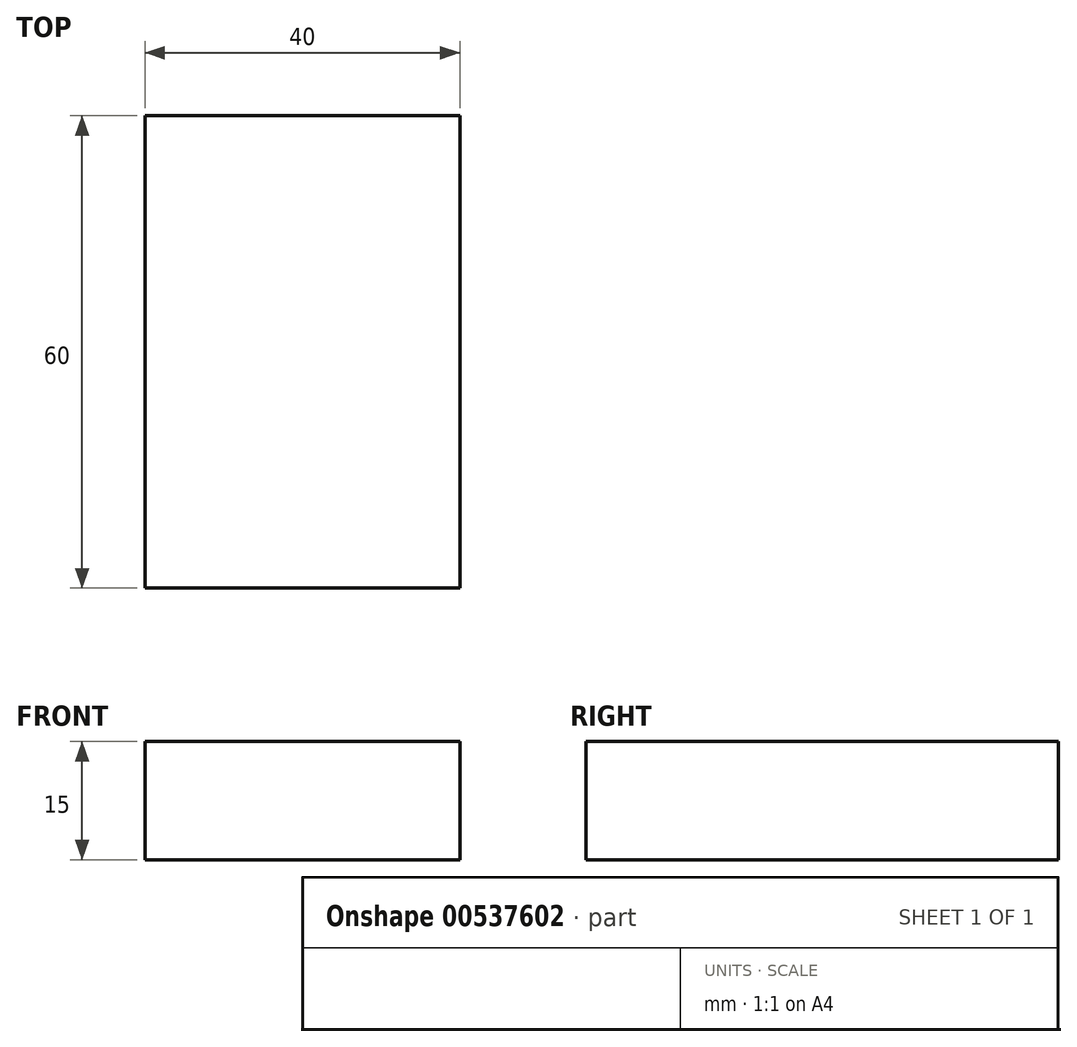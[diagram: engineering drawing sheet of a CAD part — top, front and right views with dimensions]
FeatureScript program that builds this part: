
annotation { "Feature Type Name" : "Feature", "Feature Type Description" : "" }
export const myFeature = defineFeature(function(context is Context, id is Id, definition is map)
    precondition{}
    {
        {
            var Q0;
            Q0=qCreatedBy(makeId("Top.planeOp"),FACE);
            var sketch = newSketch(context, id + "F0", { "sketchPlane" : qUnion([Q0])});
            skLineSegment(sketch, "E0.bottom", {"start": v(0, 0) * mm, "end": v(40, 0) * mm});
            skLineSegment(sketch, "E0.top", {"start": v(0, -60) * mm, "end": v(40, -60) * mm});
            skLineSegment(sketch, "E0.left", {"start": v(0, 0) * mm, "end": v(0, -60) * mm});
            skLineSegment(sketch, "E0.right", {"start": v(40, 0) * mm, "end": v(40, -60) * mm});
            skSolve(sketch);
        }
        {
            var Q0;
            Q0=makeQuery(id+"F0.imprint","IMPRINT",FACE,{"disambiguationData":[TD([[makeQuery(id+"F0.imprint","IMPRINT",EDGE,{"derivedFrom":sQuery(id+"F0.wireOp",EDGE,"E0.bottom")}),-1.0]])]});
            extrude(context, id + "F1", {"entities" : qUnion([Q0]), "depth" : 15 * mm, "offsetDistance" : 25 * mm});
        }
    });
